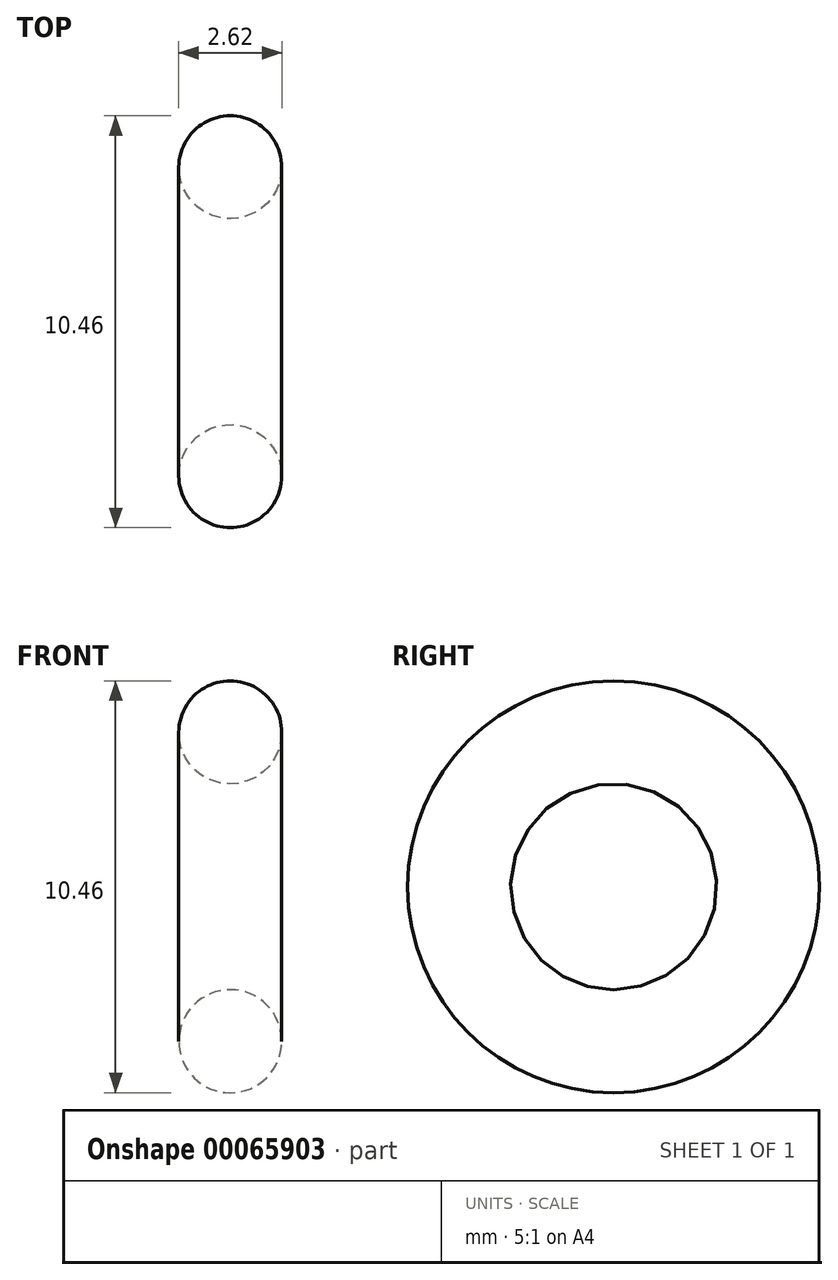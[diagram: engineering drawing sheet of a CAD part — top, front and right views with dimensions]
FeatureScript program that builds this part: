
annotation { "Feature Type Name" : "Feature", "Feature Type Description" : "" }
export const myFeature = defineFeature(function(context is Context, id is Id, definition is map)
    precondition{}
    {
        {
            var Q0;
            Q0=qCreatedBy(makeId("Front.planeOp"),FACE);
            var sketch = newSketch(context, id + "F0", { "sketchPlane" : qUnion([Q0])});
            skLineSegment(sketch, "E0", {"start": v(0, 0) * mm, "end": v(-6.06, 0) * mm, "construction": true});
            skCircle(sketch, "E1", {"center": v(0, 3.92) * mm, "radius": 1.3 * mm});
            skSolve(sketch);
        }
        {
            var Q0;
            Q0=makeQuery(id+"F0.imprint","IMPRINT",FACE,{"disambiguationData":[TD([[makeQuery(id+"F0.imprint","IMPRINT",EDGE,{"derivedFrom":sQuery(id+"F0.wireOp",EDGE,"E1")}),1.0]])]});
            var Q1;
            Q1=sQuery(id+"F0.wireOp",EDGE,"E0");
            revolve(context, id + "F1", {"entities" : qUnion([Q0]), "axis" : qUnion([Q1]), "revolveType" : RevolveType.FULL});
        }
    });
